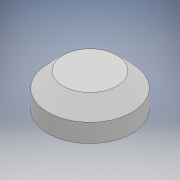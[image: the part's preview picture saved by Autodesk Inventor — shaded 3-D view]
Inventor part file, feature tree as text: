
AUTODESK INVENTOR PART (.ipt)
format: ipt  version: 2018 (Build 220112000, 112)  size: 200,704 bytes
history: native  units: mm
features: extrude x5, sketch x5, fillet x1, chamfer x1, pattern_circular x1
ambient origin geometry x8: Origin, YZ Plane, XZ Plane, XY Plane, X Axis, Y Axis, Z Axis, Center Point
bodies: Solid1 (feature_tree)
feature tree (13):
  extrude  "Extrusion1"  Depth=10.0mm TaperAngle=0.0deg
  extrude  "Extrusion2"  Depth=3.0mm TaperAngle=0.0deg
  extrude  "Extrusion3"  Depth=6.0mm TaperAngle=0.0deg
  extrude  "Extrusion4"  Depth=2.0mm TaperAngle=0.0deg
  fillet  "Fillet2"  Radius=0.7mm
  extrude  "Extrusion5"  Depth=0.6mm
  chamfer  "Chamfer1"  Distance=5.0mm
  pattern_circular  "Circular Pattern2"  [2 undecoded]
  sketch  "Sketch1"  dims[d0=25.0mm d1=10.0mm d2=0.0mm]
  sketch  "Sketch2"  dims[d3=24.0mm d4=3.0mm d5=0.0mm]
  sketch  "Sketch4"  dims[d6=13.5mm d7=6.0mm d8=0.0mm]
  sketch  "Sketch5"  dims[d10=0.7mm d11=2.0mm d12=0.0mm d13=0.7mm]
  sketch  "Sketch6"  dims[d14=1.0mm d15=0.6mm d16=5.0mm d17=5.0mm d18=0.0mm d22=4.5mm d23=2.0mm d24=45.0deg d25=60.0mm d26=360.0deg]
note: 2 required parameter values undecoded (feature->parameter linkage not recoverable at this tier; creation-order binding heuristic only, values carry confidence <= 0.55)
